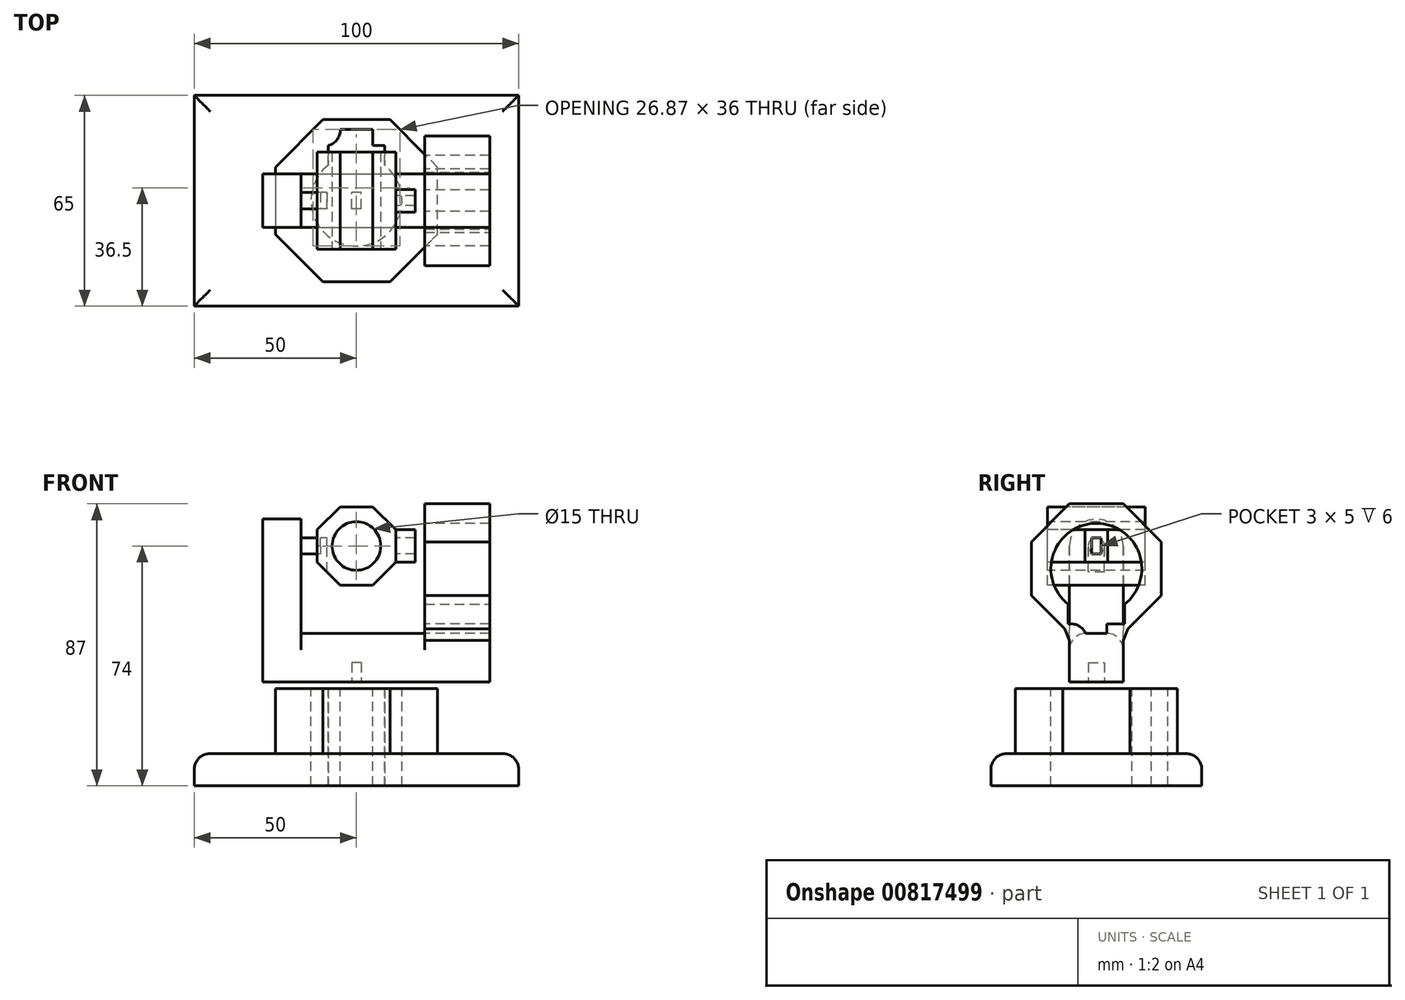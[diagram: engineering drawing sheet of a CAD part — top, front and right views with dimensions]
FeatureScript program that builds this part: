
annotation { "Feature Type Name" : "Feature", "Feature Type Description" : "" }
export const myFeature = defineFeature(function(context is Context, id is Id, definition is map)
    precondition{}
    {
        {
            var Q0;
            Q0=qCreatedBy(makeId("Front.planeOp"),FACE);
            var sketch = newSketch(context, id + "F0", { "sketchPlane" : qUnion([Q0])});
            skCircle(sketch, "E0", {"center": v(0, 0) * mm, "radius": 7.5 * mm});
            skCircle(sketch, "E1.cCircle", {"center": v(0, 0) * mm, "radius": 12.07 * mm, "construction": true});
            skLineSegment(sketch, "E1.0", {"start": v(-5, 12.07) * mm, "end": v(5, 12.07) * mm});
            skLineSegment(sketch, "E1.1", {"start": v(5, 12.07) * mm, "end": v(12.07, 5) * mm});
            skLineSegment(sketch, "E1.2", {"start": v(12.07, 5) * mm, "end": v(12.07, -5) * mm});
            skLineSegment(sketch, "E1.3", {"start": v(12.07, -5) * mm, "end": v(5, -12.07) * mm});
            skLineSegment(sketch, "E1.4", {"start": v(5, -12.07) * mm, "end": v(-5, -12.07) * mm});
            skLineSegment(sketch, "E1.5", {"start": v(-5, -12.07) * mm, "end": v(-12.07, -5) * mm});
            skLineSegment(sketch, "E1.6", {"start": v(-12.07, -5) * mm, "end": v(-12.07, 5) * mm});
            skLineSegment(sketch, "E1.7", {"start": v(-12.07, 5) * mm, "end": v(-5, 12.07) * mm});
            skPoint(sketch, "E1.0.midPoint", {"position": v(0, 12.07) * mm});
            skSolve(sketch);
        }
        {
            var Q0;
            Q0=makeQuery(id+"F0.imprint","IMPRINT",FACE,{"disambiguationData":[TD([[makeQuery(id+"F0.imprint","IMPRINT",EDGE,{"derivedFrom":sQuery(id+"F0.wireOp",EDGE,"E0")}),-1.0]])]});
            extrude(context, id + "F1", {"entities" : qUnion([Q0]), "endBound" : BoundingType.SYMMETRIC, "oppositeDirection" : true, "depth" : 30 * mm, "offsetDistance" : 25 * mm});
        }
        {
            var Q0;
            Q0=makeQuery(id+"F1.opExtrude","SWEPT_FACE",FACE,{"disambiguationData":[OSD([sQuery(id+"F0.wireOp",EDGE,"E1.2")])]});
            var sketch = newSketch(context, id + "F2", { "sketchPlane" : qUnion([Q0])});
            skLineSegment(sketch, "E2.bottom", {"start": v(1.5, 2.5) * mm, "end": v(-1.5, 2.5) * mm});
            skLineSegment(sketch, "E2.top", {"start": v(1.5, -2.5) * mm, "end": v(-1.5, -2.5) * mm});
            skLineSegment(sketch, "E2.left", {"start": v(1.5, 2.5) * mm, "end": v(1.5, -2.5) * mm});
            skLineSegment(sketch, "E2.right", {"start": v(-1.5, 2.5) * mm, "end": v(-1.5, -2.5) * mm});
            skPoint(sketch, "E2.middle", {"position": v(0, 0) * mm});
            skLineSegment(sketch, "E3.bottom", {"start": v(3.5, 5) * mm, "end": v(-3.5, 5) * mm});
            skLineSegment(sketch, "E3.top", {"start": v(3.5, -5) * mm, "end": v(-3.5, -5) * mm});
            skLineSegment(sketch, "E3.left", {"start": v(3.5, 5) * mm, "end": v(3.5, -5) * mm});
            skLineSegment(sketch, "E3.right", {"start": v(-3.5, 5) * mm, "end": v(-3.5, -5) * mm});
            skSolve(sketch);
        }
        {
            var Q0;
            Q0=makeQuery(id+"F2.imprint","IMPRINT",FACE,{"disambiguationData":[TD([[makeQuery(id+"F2.imprint","IMPRINT",EDGE,{"derivedFrom":sQuery(id+"F2.wireOp",EDGE,"E2.bottom")}),-1.0]])]});
            extrude(context, id + "F3", {"entities" : qUnion([Q0]), "operationType" : NewBodyOperationType.ADD, "depth" : 6 * mm, "offsetDistance" : 25 * mm});
        }
        {
            var Q0;
            Q0=makeQuery(id+"F3.opExtrude","CAP_FACE",FACE,{"disambiguationData":[OSD([sQuery(id+"F2.wireOp",EDGE,"E2.bottom"),sQuery(id+"F2.wireOp",EDGE,"E2.top"),sQuery(id+"F2.wireOp",EDGE,"E2.left"),sQuery(id+"F2.wireOp",EDGE,"E2.right"),sQuery(id+"F2.wireOp",EDGE,"E3.bottom"),sQuery(id+"F2.wireOp",EDGE,"E3.top"),sQuery(id+"F2.wireOp",EDGE,"E3.left"),sQuery(id+"F2.wireOp",EDGE,"E3.right")])],"isStart":false});
            var Q1;
            Q1 = qBodyType(qCreatedBy(id + "F5" ,EDGE), BodyType.WIRE);
            cPlane(context, id + "F4", {"entities" : qUnion([Q0, Q1]), "cplaneType" : CPlaneType.OFFSET, "offset" : 3 * mm, "width" : 150 * mm, "height" : 150 * mm});
        }
        {
            var Q0;
            Q0=qCreatedBy(id+"F4.planeOp",FACE);
            var sketch = newSketch(context, id + "F5", { "sketchPlane" : qUnion([Q0])});
            skCircle(sketch, "E4", {"center": v(0, -7) * mm, "radius": 14 * mm});
            skCircle(sketch, "E5.cCircle", {"center": v(0, -7) * mm, "radius": 20 * mm, "construction": true});
            skLineSegment(sketch, "E5.0", {"start": v(-8.28, 13) * mm, "end": v(8.28, 13) * mm});
            skLineSegment(sketch, "E5.1", {"start": v(8.28, 13) * mm, "end": v(20, 1.28) * mm});
            skLineSegment(sketch, "E5.2", {"start": v(20, 1.28) * mm, "end": v(20, -15.28) * mm});
            skLineSegment(sketch, "E5.3", {"start": v(20, -15.28) * mm, "end": v(8.28, -27) * mm});
            skLineSegment(sketch, "E5.4", {"start": v(8.28, -27) * mm, "end": v(-8.28, -27) * mm});
            skLineSegment(sketch, "E5.5", {"start": v(-8.28, -27) * mm, "end": v(-20, -15.28) * mm});
            skLineSegment(sketch, "E5.6", {"start": v(-20, -15.28) * mm, "end": v(-20, 1.28) * mm});
            skLineSegment(sketch, "E5.7", {"start": v(-20, 1.28) * mm, "end": v(-8.28, 13) * mm});
            skPoint(sketch, "E5.0.midPoint", {"position": v(0, 13) * mm});
            skSolve(sketch);
        }
        {
            var Q0;
            Q0=makeQuery(id+"F5.imprint","IMPRINT",FACE,{"disambiguationData":[TD([[makeQuery(id+"F5.imprint","IMPRINT",EDGE,{"derivedFrom":sQuery(id+"F5.wireOp",EDGE,"E4")}),-1.0]])]});
            extrude(context, id + "F6", {"entities" : qUnion([Q0]), "flatOperationType" : FlatOperationType.REMOVE, "depth" : 20 * mm, "offsetDistance" : 25 * mm, "domain" : OperationDomain.MODEL});
        }
        {
            var Q0;
            Q0=makeQuery(id+"F6.opExtrude","CAP_FACE",FACE,{"disambiguationData":[OSD([sQuery(id+"F5.wireOp",EDGE,"E4"),sQuery(id+"F5.wireOp",EDGE,"E5.0"),sQuery(id+"F5.wireOp",EDGE,"E5.1"),sQuery(id+"F5.wireOp",EDGE,"E5.2"),sQuery(id+"F5.wireOp",EDGE,"E5.3"),sQuery(id+"F5.wireOp",EDGE,"E5.4"),sQuery(id+"F5.wireOp",EDGE,"E5.5"),sQuery(id+"F5.wireOp",EDGE,"E5.6"),sQuery(id+"F5.wireOp",EDGE,"E5.7")])],"isStart":false});
            var sketch = newSketch(context, id + "F7", { "sketchPlane" : qUnion([Q0])});
            skLineSegment(sketch, "E6.bottom", {"start": v(8.75, -24) * mm, "end": v(-8.75, -24) * mm});
            skLineSegment(sketch, "E6.top", {"start": v(8.75, -18) * mm, "end": v(-8.75, -18) * mm});
            skLineSegment(sketch, "E6.left", {"start": v(8.75, -24) * mm, "end": v(8.75, -18) * mm});
            skLineSegment(sketch, "E6.right", {"start": v(-8.75, -24) * mm, "end": v(-8.75, -18) * mm});
            skPoint(sketch, "E6.middle", {"position": v(0, -21) * mm});
            skPoint(sketch, "E7", {"position": v(0, 7) * mm});
            skSolve(sketch);
        }
        {
            var Q0;
            Q0=makeQuery(id+"F7.imprint","IMPRINT",FACE,{"disambiguationData":[TD([[makeQuery(id+"F7.imprint","IMPRINT",EDGE,{"derivedFrom":sQuery(id+"F7.wireOp",EDGE,"E6.bottom")}),-1.0]])]});
            var Q1;
            Q1=makeQuery(id+"F6.opExtrude","CAP_FACE",FACE,{"disambiguationData":[OSD([sQuery(id+"F5.wireOp",EDGE,"E4"),sQuery(id+"F5.wireOp",EDGE,"E5.0"),sQuery(id+"F5.wireOp",EDGE,"E5.1"),sQuery(id+"F5.wireOp",EDGE,"E5.2"),sQuery(id+"F5.wireOp",EDGE,"E5.3"),sQuery(id+"F5.wireOp",EDGE,"E5.4"),sQuery(id+"F5.wireOp",EDGE,"E5.5"),sQuery(id+"F5.wireOp",EDGE,"E5.6"),sQuery(id+"F5.wireOp",EDGE,"E5.7")])],"isStart":true});
            extrude(context, id + "F8", {"entities" : qUnion([Q0]), "operationType" : NewBodyOperationType.REMOVE, "endBound" : BoundingType.UP_TO_SURFACE, "oppositeDirection" : true, "depth" : 25 * mm, "endBoundEntityFace" : qUnion([Q1]), "offsetDistance" : 25 * mm});
        }
        {
            var Q0;
            Q0=makeQuery(id+"F6.opExtrude","CAP_FACE",FACE,{"disambiguationData":[OSD([sQuery(id+"F5.wireOp",EDGE,"E4"),sQuery(id+"F5.wireOp",EDGE,"E5.0"),sQuery(id+"F5.wireOp",EDGE,"E5.1"),sQuery(id+"F5.wireOp",EDGE,"E5.2"),sQuery(id+"F5.wireOp",EDGE,"E5.3"),sQuery(id+"F5.wireOp",EDGE,"E5.4"),sQuery(id+"F5.wireOp",EDGE,"E5.5"),sQuery(id+"F5.wireOp",EDGE,"E5.6"),sQuery(id+"F5.wireOp",EDGE,"E5.7")])],"isStart":false});
            var sketch = newSketch(context, id + "F9", { "sketchPlane" : qUnion([Q0])});
            skLineSegment(sketch, "E8.bottom", {"start": v(-8.28, -27) * mm, "end": v(8.28, -27) * mm});
            skLineSegment(sketch, "E8.top", {"start": v(-8.28, -42) * mm, "end": v(8.28, -42) * mm});
            skLineSegment(sketch, "E8.left", {"start": v(-8.28, -27) * mm, "end": v(-8.28, -42) * mm});
            skLineSegment(sketch, "E8.right", {"start": v(8.28, -27) * mm, "end": v(8.28, -42) * mm});
            skSolve(sketch);
        }
        {
            var Q0;
            Q0=makeQuery(id+"F9.imprint","IMPRINT",FACE,{"disambiguationData":[TD([[makeQuery(id+"F9.imprint","IMPRINT",EDGE,{"derivedFrom":sQuery(id+"F9.wireOp",EDGE,"E8.bottom")}),1.0]])]});
            extrude(context, id + "F10", {"entities" : qUnion([Q0]), "operationType" : NewBodyOperationType.ADD, "oppositeDirection" : true, "depth" : 70 * mm, "offsetDistance" : 25 * mm});
        }
        {
            var Q0;
            Q0=makeQuery(id+"F10.opExtrude","CAP_FACE",FACE,{"disambiguationData":[OSD([sQuery(id+"F9.wireOp",EDGE,"E8.bottom"),sQuery(id+"F9.wireOp",EDGE,"E8.top"),sQuery(id+"F9.wireOp",EDGE,"E8.left"),sQuery(id+"F9.wireOp",EDGE,"E8.right")])],"isStart":false});
            var sketch = newSketch(context, id + "F11", { "sketchPlane" : qUnion([Q0])});
            skLineSegment(sketch, "E9.bottom", {"start": v(-8.28, -42) * mm, "end": v(8.28, -42) * mm});
            skLineSegment(sketch, "E9.top", {"start": v(-8.28, 0) * mm, "end": v(8.28, 0) * mm, "construction": true});
            skLineSegment(sketch, "E9.left", {"start": v(-8.28, -42) * mm, "end": v(-8.28, 0) * mm});
            skLineSegment(sketch, "E9.right", {"start": v(8.28, -42) * mm, "end": v(8.28, 0) * mm});
            skArc(sketch, "E10", {"start": v(8.28, 0) * mm, "mid": v(0, 8.28) * mm, "end": v(-8.28, 0) * mm});
            skSolve(sketch);
        }
        {
            var Q0;
            {var subQ2=sQuery(id+"F11.wireOp",EDGE,"E10");Q0=makeQuery(id+"F11.imprint","IMPRINT",FACE,{"disambiguationData":[TD([[makeQuery(id+"F11.imprint","IMPRINT",EDGE,{"derivedFrom":subQ2}),1.0]])]});}
            var Q1;
            Q1=makeQuery(id+"F1.opExtrude","SWEPT_FACE",FACE,{"disambiguationData":[OSD([sQuery(id+"F0.wireOp",EDGE,"E1.6")])]});
            extrude(context, id + "F12", {"entities" : qUnion([Q0]), "operationType" : NewBodyOperationType.ADD, "endBound" : BoundingType.UP_TO_SURFACE, "oppositeDirection" : true, "depth" : 5 * mm, "endBoundEntityFace" : qUnion([Q1]), "hasOffset" : true, "offsetDistance" : 5 * mm});
        }
        {
            var Q0;
            Q0=makeQuery(id+"F10.opExtrude","SWEPT_FACE",FACE,{"disambiguationData":[OSD([sQuery(id+"F9.wireOp",EDGE,"E8.top")])]});
            var sketch = newSketch(context, id + "F13", { "sketchPlane" : qUnion([Q0])});
            skLineSegment(sketch, "E11.bottom", {"start": v(1.5, 2.5) * mm, "end": v(-1.5, 2.5) * mm});
            skLineSegment(sketch, "E11.top", {"start": v(1.5, -2.5) * mm, "end": v(-1.5, -2.5) * mm});
            skLineSegment(sketch, "E11.left", {"start": v(1.5, 2.5) * mm, "end": v(1.5, -2.5) * mm});
            skLineSegment(sketch, "E11.right", {"start": v(-1.5, 2.5) * mm, "end": v(-1.5, -2.5) * mm});
            skPoint(sketch, "E11.middle", {"position": v(0, 0) * mm});
            skSolve(sketch);
        }
        {
            var Q0;
            Q0=makeQuery(id+"F13.imprint","IMPRINT",FACE,{"disambiguationData":[TD([[makeQuery(id+"F13.imprint","IMPRINT",EDGE,{"derivedFrom":sQuery(id+"F13.wireOp",EDGE,"E11.bottom")}),1.0]])]});
            var Q1;
            Q1=makeQuery(id+"F10.opExtrude","SWEPT_FACE",FACE,{"disambiguationData":[OSD([sQuery(id+"F9.wireOp",EDGE,"E8.bottom")])]});
            extrude(context, id + "F14", {"entities" : qUnion([Q0]), "operationType" : NewBodyOperationType.REMOVE, "oppositeDirection" : true, "depth" : 6 * mm, "endBoundEntityFace" : qUnion([Q1]), "hasOffset" : true, "offsetDistance" : 2 * mm});
        }
        {
            var Q0;
            Q0=makeQuery(id+"F10.opExtrude","SWEPT_FACE",FACE,{"disambiguationData":[OSD([sQuery(id+"F9.wireOp",EDGE,"E8.top")])]});
            cPlane(context, id + "F15", {"entities" : qUnion([Q0]), "cplaneType" : CPlaneType.OFFSET, "offset" : 2 * mm, "width" : 150 * mm, "height" : 150 * mm});
        }
        {
            var Q0;
            Q0=qCreatedBy(id+"F15.planeOp",FACE);
            var sketch = newSketch(context, id + "F16", { "sketchPlane" : qUnion([Q0])});
            skCircle(sketch, "E12", {"center": v(0, 0) * mm, "radius": 14 * mm});
            skCircle(sketch, "E13.cCircle", {"center": v(0, 0) * mm, "radius": 25 * mm, "construction": true});
            skLineSegment(sketch, "E13.0", {"start": v(-10.36, 25) * mm, "end": v(10.36, 25) * mm});
            skLineSegment(sketch, "E13.1", {"start": v(10.36, 25) * mm, "end": v(25, 10.36) * mm});
            skLineSegment(sketch, "E13.2", {"start": v(25, 10.36) * mm, "end": v(25, -10.36) * mm});
            skLineSegment(sketch, "E13.3", {"start": v(25, -10.36) * mm, "end": v(10.36, -25) * mm});
            skLineSegment(sketch, "E13.4", {"start": v(10.36, -25) * mm, "end": v(-10.36, -25) * mm});
            skLineSegment(sketch, "E13.5", {"start": v(-10.36, -25) * mm, "end": v(-25, -10.36) * mm});
            skLineSegment(sketch, "E13.6", {"start": v(-25, -10.36) * mm, "end": v(-25, 10.36) * mm});
            skLineSegment(sketch, "E13.7", {"start": v(-25, 10.36) * mm, "end": v(-10.36, 25) * mm});
            skPoint(sketch, "E13.0.midPoint", {"position": v(0, 25) * mm});
            skSolve(sketch);
        }
        {
            var Q0;
            Q0=makeQuery(id+"F16.imprint","IMPRINT",FACE,{"disambiguationData":[TD([[makeQuery(id+"F16.imprint","IMPRINT",EDGE,{"derivedFrom":sQuery(id+"F16.wireOp",EDGE,"ab7be03b-d63e-4127-b53d-c97241b83293.bottom")}),-1.0]])]});
            var Q1;
            Q1=makeQuery(id+"F16.imprint","IMPRINT",FACE,{"disambiguationData":[TD([[makeQuery(id+"F16.imprint","IMPRINT",EDGE,{"derivedFrom":sQuery(id+"F16.wireOp",EDGE,"E12")}),-1.0]])]});
            extrude(context, id + "F17", {"entities" : qUnion([Q0, Q1]), "depth" : 20 * mm, "offsetDistance" : 25 * mm});
        }
        {
            var Q0;
            Q0=makeQuery(id+"F17.opExtrude","CAP_FACE",FACE,{"disambiguationData":[OSD([sQuery(id+"F16.wireOp",EDGE,"E12"),sQuery(id+"F16.wireOp",EDGE,"E13.0"),sQuery(id+"F16.wireOp",EDGE,"E13.1"),sQuery(id+"F16.wireOp",EDGE,"E13.2"),sQuery(id+"F16.wireOp",EDGE,"E13.3"),sQuery(id+"F16.wireOp",EDGE,"E13.4"),sQuery(id+"F16.wireOp",EDGE,"E13.5"),sQuery(id+"F16.wireOp",EDGE,"E13.6"),sQuery(id+"F16.wireOp",EDGE,"E13.7")])],"isStart":false});
            var sketch = newSketch(context, id + "F18", { "sketchPlane" : qUnion([Q0])});
            skLineSegment(sketch, "E14.bottom", {"start": v(8.75, -17) * mm, "end": v(-8.75, -17) * mm});
            skLineSegment(sketch, "E14.top", {"start": v(8.75, -11) * mm, "end": v(-8.75, -11) * mm});
            skLineSegment(sketch, "E14.left", {"start": v(8.75, -17) * mm, "end": v(8.75, -11) * mm});
            skLineSegment(sketch, "E14.right", {"start": v(-8.75, -17) * mm, "end": v(-8.75, -11) * mm});
            skPoint(sketch, "E14.middle", {"position": v(0, -14) * mm});
            skPoint(sketch, "E15", {"position": v(-27.27, 14.01) * mm});
            skSolve(sketch);
        }
        {
            var Q0;
            Q0 = qSketchRegion(id + "F18", true);
            var Q1;
            Q1=makeQuery(id+"F17.opExtrude","CAP_FACE",FACE,{"disambiguationData":[OSD([sQuery(id+"F16.wireOp",EDGE,"E12"),sQuery(id+"F16.wireOp",EDGE,"E13.0"),sQuery(id+"F16.wireOp",EDGE,"E13.1"),sQuery(id+"F16.wireOp",EDGE,"E13.2"),sQuery(id+"F16.wireOp",EDGE,"E13.3"),sQuery(id+"F16.wireOp",EDGE,"E13.4"),sQuery(id+"F16.wireOp",EDGE,"E13.5"),sQuery(id+"F16.wireOp",EDGE,"E13.6"),sQuery(id+"F16.wireOp",EDGE,"E13.7")])],"isStart":true});
            extrude(context, id + "F19", {"entities" : qUnion([Q0]), "operationType" : NewBodyOperationType.REMOVE, "endBound" : BoundingType.UP_TO_SURFACE, "oppositeDirection" : true, "depth" : 25 * mm, "endBoundEntityFace" : qUnion([Q1]), "offsetDistance" : 25 * mm});
        }
        {
            var Q0;
            Q0=makeQuery(id+"F1.opExtrude","SWEPT_FACE",FACE,{"disambiguationData":[OSD([sQuery(id+"F0.wireOp",EDGE,"E1.6")])]});
            var sketch = newSketch(context, id + "F20", { "sketchPlane" : qUnion([Q0])});
            skCircle(sketch, "E16", {"center": v(0, 0) * mm, "radius": 2.5 * mm});
            skSolve(sketch);
        }
        {
            var Q0;
            Q0=makeQuery(id+"F20.imprint","IMPRINT",FACE,{"disambiguationData":[TD([[makeQuery(id+"F20.imprint","IMPRINT",EDGE,{"derivedFrom":sQuery(id+"F20.wireOp",EDGE,"E16")}),1.0]])]});
            var Q1;
            Q1=makeQuery(id+"F1.opExtrude","SWEPT_FACE",FACE,{"disambiguationData":[OSD([sQuery(id+"F0.wireOp",EDGE,"E0")])]});
            extrude(context, id + "F21", {"entities" : qUnion([Q0]), "operationType" : NewBodyOperationType.REMOVE, "oppositeDirection" : true, "depth" : 3 * mm, "endBoundEntityFace" : qUnion([Q1]), "offsetDistance" : 1 * mm});
        }
        {
            var Q0;
            Q0=makeQuery(id+"F12.opExtrude","CAP_FACE",FACE,{"disambiguationData":[OSD([sQuery(id+"F9.wireOp",EDGE,"E8.bottom"),sQuery(id+"F11.wireOp",EDGE,"E9.left"),sQuery(id+"F11.wireOp",EDGE,"E9.right"),sQuery(id+"F11.wireOp",EDGE,"E10")])],"isStart":false});
            var sketch = newSketch(context, id + "F22", { "sketchPlane" : qUnion([Q0])});
            skCircle(sketch, "E17", {"center": v(0, 0) * mm, "radius": 2.5 * mm});
            skSolve(sketch);
        }
        {
            var Q0;
            Q0 = qSketchRegion(id + "F22", true);
            var Q1;
            Q1=sQuery(id+"F22.wireOp",EDGE,"E17");
            var Q2;
            Q2=makeQuery(id+"F21.boolean.opBoolean","COPY",FACE,{"derivedFrom":makeQuery(id+"F21.opExtrude","CAP_FACE",FACE,{"disambiguationData":[OSD([sQuery(id+"F20.wireOp",EDGE,"E16")])],"isStart":false})});
            extrude(context, id + "F23", {"entities" : qUnion([Q0]), "operationType" : NewBodyOperationType.ADD, "surfaceEntities" : qUnion([Q1]), "endBound" : BoundingType.UP_TO_SURFACE, "depth" : 25 * mm, "endBoundEntityFace" : qUnion([Q2]), "hasOffset" : true, "offsetDistance" : 2 * mm});
        }
        {
            var Q0;
            Q0=makeQuery(id+"F1.opExtrude","SWEPT_FACE",FACE,{"disambiguationData":[OSD([sQuery(id+"F0.wireOp",EDGE,"E1.6")])]});
            var sketch = newSketch(context, id + "F24", { "sketchPlane" : qUnion([Q0])});
            skLineSegment(sketch, "E18.bottom", {"start": v(-2.5, 0) * mm, "end": v(2.5, 0) * mm});
            skLineSegment(sketch, "E18.top", {"start": v(-2.5, -12.07) * mm, "end": v(2.5, -12.07) * mm});
            skLineSegment(sketch, "E18.left", {"start": v(-2.5, 0) * mm, "end": v(-2.5, -12.07) * mm});
            skLineSegment(sketch, "E18.right", {"start": v(2.5, 0) * mm, "end": v(2.5, -12.07) * mm});
            skSolve(sketch);
        }
        {
            var Q0;
            {var subQ0=sQuery(id+"F24.wireOp",EDGE,"E18.left");var subQ1=sQuery(id+"F24.wireOp",EDGE,"E18.bottom");var subQ2=makeQuery(id+"F21.boolean.opBoolean","COPY",EDGE,{"derivedFrom":makeQuery(id+"F21.opExtrude","CAP_EDGE",EDGE,{"disambiguationData":[OSD([sQuery(id+"F20.wireOp",EDGE,"E16")])],"isStart":true})});var subQ3=makeQuery(id+"F24.imprint","INTERSECT",VERTEX,{"derivedFrom":[subQ2,subQ1,subQ0]});Q0=makeQuery(id+"F24.imprint","IMPRINT",FACE,{"disambiguationData":[TD([[makeQuery(id+"F24.imprint","IMPRINT",EDGE,{"disambiguationData":[TD([[subQ3,-1.0]])],"derivedFrom":subQ0}),1.0]])]});}
            var Q1;
            {var subQ0=sQuery(id+"F24.wireOp",EDGE,"E18.top");Q1=makeQuery(id+"F24.imprint","IMPRINT",FACE,{"disambiguationData":[TD([[makeQuery(id+"F24.imprint","IMPRINT",EDGE,{"derivedFrom":subQ0}),1.0]])]});}
            var Q2;
            Q2=makeQuery(id+"F21.boolean.opBoolean","COPY",FACE,{"derivedFrom":makeQuery(id+"F21.opExtrude","CAP_FACE",FACE,{"disambiguationData":[OSD([sQuery(id+"F20.wireOp",EDGE,"E16")])],"isStart":false})});
            extrude(context, id + "F25", {"entities" : qUnion([Q0, Q1]), "operationType" : NewBodyOperationType.REMOVE, "endBound" : BoundingType.UP_TO_SURFACE, "oppositeDirection" : true, "depth" : 25 * mm, "endBoundEntityFace" : qUnion([Q2]), "offsetDistance" : 25 * mm});
        }
        {
            var Q0;
            Q0=makeQuery(id+"F17.opExtrude","CAP_FACE",FACE,{"disambiguationData":[OSD([sQuery(id+"F16.wireOp",EDGE,"E12"),sQuery(id+"F16.wireOp",EDGE,"E13.0"),sQuery(id+"F16.wireOp",EDGE,"E13.1"),sQuery(id+"F16.wireOp",EDGE,"E13.2"),sQuery(id+"F16.wireOp",EDGE,"E13.3"),sQuery(id+"F16.wireOp",EDGE,"E13.4"),sQuery(id+"F16.wireOp",EDGE,"E13.5"),sQuery(id+"F16.wireOp",EDGE,"E13.6"),sQuery(id+"F16.wireOp",EDGE,"E13.7")])],"isStart":false});
            var sketch = newSketch(context, id + "F26", { "sketchPlane" : qUnion([Q0])});
            skLineSegment(sketch, "E19.bottom", {"start": v(50, 32.5) * mm, "end": v(-50, 32.5) * mm});
            skLineSegment(sketch, "E19.top", {"start": v(50, -32.5) * mm, "end": v(-50, -32.5) * mm});
            skLineSegment(sketch, "E19.left", {"start": v(50, 32.5) * mm, "end": v(50, -32.5) * mm});
            skLineSegment(sketch, "E19.right", {"start": v(-50, 32.5) * mm, "end": v(-50, -32.5) * mm});
            skPoint(sketch, "E19.middle", {"position": v(0, 0) * mm});
            skSolve(sketch);
        }
        {
            var Q0;
            Q0=makeQuery(id+"F26.imprint","IMPRINT",FACE,{"disambiguationData":[TD([[makeQuery(id+"F26.imprint","IMPRINT",EDGE,{"derivedFrom":sQuery(id+"F26.wireOp",EDGE,"E19.bottom")}),1.0]])]});
            var Q1;
            {var subQ5=sQuery(id+"F16.wireOp",EDGE,"E13.0");Q1=makeQuery(id+"F26.imprint","IMPRINT",FACE,{"disambiguationData":[TD([[makeQuery(id+"F26.imprint","IMPRINT",EDGE,{"derivedFrom":makeQuery(id+"F17.opExtrude","CAP_EDGE",EDGE,{"disambiguationData":[OSD([subQ5])],"isStart":false})}),-1.0]])]});}
            extrude(context, id + "F27", {"entities" : qUnion([Q0, Q1]), "operationType" : NewBodyOperationType.ADD, "depth" : 10 * mm, "offsetDistance" : 25 * mm});
        }
        {
            var Q0;
            Q0=makeQuery(id+"F27.opExtrude","CAP_EDGE",EDGE,{"disambiguationData":[OSD([sQuery(id+"F26.wireOp",EDGE,"E19.left")])],"isStart":true});
            var Q1;
            Q1=makeQuery(id+"F27.opExtrude","CAP_EDGE",EDGE,{"disambiguationData":[OSD([sQuery(id+"F26.wireOp",EDGE,"E19.bottom")])],"isStart":true});
            var Q2;
            Q2=makeQuery(id+"F27.opExtrude","CAP_EDGE",EDGE,{"disambiguationData":[OSD([sQuery(id+"F26.wireOp",EDGE,"E19.right")])],"isStart":true});
            var Q3;
            Q3=makeQuery(id+"F27.opExtrude","CAP_EDGE",EDGE,{"disambiguationData":[OSD([sQuery(id+"F26.wireOp",EDGE,"E19.top")])],"isStart":true});
            fillet(context, id + "F28", {"entities" : qUnion([Q0, Q1, Q2, Q3]), "radius" : 5 * mm, "tangentPropagation" : true, "allowEdgeOverflow" : false});
        }
        {
            var Q0;
            Q0=makeQuery(id+"F10.boolean.opBoolean","SPLIT",EDGE,{"derivedFrom":makeQuery(id+"F10.opExtrude","SWEPT_EDGE",EDGE,{"disambiguationData":[OSD([sQuery(id+"F5.wireOp",EDGE,"E5.5"),sQuery(id+"F9.wireOp",EDGE,"E8.bottom"),sQuery(id+"F9.wireOp",EDGE,"E8.left")])]})});
            var Q1;
            Q1=makeQuery(id+"F10.boolean.opBoolean","SPLIT",EDGE,{"derivedFrom":makeQuery(id+"F10.opExtrude","SWEPT_EDGE",EDGE,{"disambiguationData":[OSD([sQuery(id+"F5.wireOp",EDGE,"E5.3"),sQuery(id+"F9.wireOp",EDGE,"E8.bottom"),sQuery(id+"F9.wireOp",EDGE,"E8.right")])]})});
            fillet(context, id + "F29", {"entities" : qUnion([Q0, Q1]), "radius" : 5 * mm, "tangentPropagation" : true, "allowEdgeOverflow" : false});
        }
        {
            var Q0;
            {var subQ0=sQuery(id+"F5.wireOp",EDGE,"E5.3");Q0=makeQuery(id+"F10.boolean.opBoolean","MERGE",EDGE,{"derivedFrom":[makeQuery(id+"F6.opExtrude","SWEPT_EDGE",EDGE,{"disambiguationData":[OSD([subQ0,sQuery(id+"F5.wireOp",EDGE,"E5.4")])]}),makeQuery(id+"F10.opExtrude","SWEPT_EDGE",EDGE,{"disambiguationData":[OSD([subQ0,sQuery(id+"F9.wireOp",EDGE,"E8.bottom"),sQuery(id+"F9.wireOp",EDGE,"E8.right")])]})]});}
            var Q1;
            {var subQ0=sQuery(id+"F5.wireOp",EDGE,"E5.5");Q1=makeQuery(id+"F10.boolean.opBoolean","MERGE",EDGE,{"derivedFrom":[makeQuery(id+"F6.opExtrude","SWEPT_EDGE",EDGE,{"disambiguationData":[OSD([sQuery(id+"F5.wireOp",EDGE,"E5.4"),subQ0])]}),makeQuery(id+"F10.opExtrude","SWEPT_EDGE",EDGE,{"disambiguationData":[OSD([subQ0,sQuery(id+"F9.wireOp",EDGE,"E8.bottom"),sQuery(id+"F9.wireOp",EDGE,"E8.left")])]})]});}
            chamfer(context, id + "F30", {"entities" : qUnion([Q0, Q1]), "width" : 5 * mm, "tangentPropagation" : true});
        }
        {
            var Q0;
            Q0=makeQuery(id+"F6.opExtrude","CAP_FACE",FACE,{"disambiguationData":[OSD([sQuery(id+"F5.wireOp",EDGE,"E4"),sQuery(id+"F5.wireOp",EDGE,"E5.0"),sQuery(id+"F5.wireOp",EDGE,"E5.1"),sQuery(id+"F5.wireOp",EDGE,"E5.2"),sQuery(id+"F5.wireOp",EDGE,"E5.3"),sQuery(id+"F5.wireOp",EDGE,"E5.4"),sQuery(id+"F5.wireOp",EDGE,"E5.5"),sQuery(id+"F5.wireOp",EDGE,"E5.6"),sQuery(id+"F5.wireOp",EDGE,"E5.7")])],"isStart":true});
            var sketch = newSketch(context, id + "F31", { "sketchPlane" : qUnion([Q0])});
            skLineSegment(sketch, "E20.bottom", {"start": v(-3.28, -24) * mm, "end": v(3.28, -24) * mm});
            skLineSegment(sketch, "E20.top", {"start": v(-3.28, -27) * mm, "end": v(3.28, -27) * mm});
            skLineSegment(sketch, "E20.left", {"start": v(-3.28, -24) * mm, "end": v(-3.28, -27) * mm});
            skLineSegment(sketch, "E20.right", {"start": v(3.28, -24) * mm, "end": v(3.28, -27) * mm});
            skSolve(sketch);
        }
        {
            var Q0;
            Q0 = qSketchRegion(id + "F31", true);
            var Q1;
            Q1=makeQuery(id+"F10.boolean.opBoolean","MERGE",FACE,{"derivedFrom":[makeQuery(id+"F6.opExtrude","CAP_FACE",FACE,{"disambiguationData":[OSD([sQuery(id+"F5.wireOp",EDGE,"E4"),sQuery(id+"F5.wireOp",EDGE,"E5.0"),sQuery(id+"F5.wireOp",EDGE,"E5.1"),sQuery(id+"F5.wireOp",EDGE,"E5.2"),sQuery(id+"F5.wireOp",EDGE,"E5.3"),sQuery(id+"F5.wireOp",EDGE,"E5.4"),sQuery(id+"F5.wireOp",EDGE,"E5.5"),sQuery(id+"F5.wireOp",EDGE,"E5.6"),sQuery(id+"F5.wireOp",EDGE,"E5.7")])],"isStart":false}),makeQuery(id+"F10.opExtrude","CAP_FACE",FACE,{"disambiguationData":[OSD([sQuery(id+"F9.wireOp",EDGE,"E8.bottom"),sQuery(id+"F9.wireOp",EDGE,"E8.top"),sQuery(id+"F9.wireOp",EDGE,"E8.left"),sQuery(id+"F9.wireOp",EDGE,"E8.right")])],"isStart":true})]});
            extrude(context, id + "F32", {"entities" : qUnion([Q0]), "operationType" : NewBodyOperationType.REMOVE, "endBound" : BoundingType.UP_TO_SURFACE, "oppositeDirection" : true, "depth" : 25 * mm, "endBoundEntityFace" : qUnion([Q1]), "offsetDistance" : 25 * mm});
        }
        {
            var Q0;
            Q0=makeQuery(id+"F32.boolean.opBoolean","COPY",EDGE,{"derivedFrom":makeQuery(id+"F32.opExtrude","SWEPT_EDGE",EDGE,{"disambiguationData":[OSD([sQuery(id+"F7.wireOp",EDGE,"E6.bottom"),sQuery(id+"F31.wireOp",EDGE,"E20.bottom"),sQuery(id+"F31.wireOp",EDGE,"E20.left")])]})});
            var Q1;
            Q1=makeQuery(id+"F32.boolean.opBoolean","COPY",EDGE,{"derivedFrom":makeQuery(id+"F32.opExtrude","SWEPT_EDGE",EDGE,{"disambiguationData":[OSD([sQuery(id+"F7.wireOp",EDGE,"E6.bottom"),sQuery(id+"F31.wireOp",EDGE,"E20.bottom"),sQuery(id+"F31.wireOp",EDGE,"E20.right")])]})});
            fillet(context, id + "F33", {"entities" : qUnion([Q0, Q1]), "radius" : 5 * mm, "tangentPropagation" : true, "allowEdgeOverflow" : false});
        }
        {
            var Q0;
            Q0=makeQuery(id+"F17.opExtrude","CAP_FACE",FACE,{"disambiguationData":[OSD([sQuery(id+"F16.wireOp",EDGE,"E12"),sQuery(id+"F16.wireOp",EDGE,"E13.0"),sQuery(id+"F16.wireOp",EDGE,"E13.1"),sQuery(id+"F16.wireOp",EDGE,"E13.2"),sQuery(id+"F16.wireOp",EDGE,"E13.3"),sQuery(id+"F16.wireOp",EDGE,"E13.4"),sQuery(id+"F16.wireOp",EDGE,"E13.5"),sQuery(id+"F16.wireOp",EDGE,"E13.6"),sQuery(id+"F16.wireOp",EDGE,"E13.7")])],"isStart":true});
            var sketch = newSketch(context, id + "F34", { "sketchPlane" : qUnion([Q0])});
            skLineSegment(sketch, "E21.bottom", {"start": v(5, 22) * mm, "end": v(-5, 22) * mm});
            skLineSegment(sketch, "E21.top", {"start": v(5, 17) * mm, "end": v(-5, 17) * mm});
            skLineSegment(sketch, "E21.left", {"start": v(5, 22) * mm, "end": v(5, 17) * mm});
            skLineSegment(sketch, "E21.right", {"start": v(-5, 22) * mm, "end": v(-5, 17) * mm});
            skPoint(sketch, "E21.middle", {"position": v(0, 19.5) * mm});
            skSolve(sketch);
        }
        {
            var Q0;
            Q0 = qSketchRegion(id + "F34", true);
            var Q1;
            Q1=makeQuery(id+"F27.opExtrude","CAP_FACE",FACE,{"disambiguationData":[OSD([sQuery(id+"F16.wireOp",EDGE,"E12"),sQuery(id+"F18.wireOp",EDGE,"E14.bottom"),sQuery(id+"F18.wireOp",EDGE,"E14.top"),sQuery(id+"F18.wireOp",EDGE,"E14.left"),sQuery(id+"F18.wireOp",EDGE,"E14.right"),sQuery(id+"F26.wireOp",EDGE,"E19.bottom"),sQuery(id+"F26.wireOp",EDGE,"E19.top"),sQuery(id+"F26.wireOp",EDGE,"E19.left"),sQuery(id+"F26.wireOp",EDGE,"E19.right")])],"isStart":false});
            extrude(context, id + "F35", {"entities" : qUnion([Q0]), "operationType" : NewBodyOperationType.REMOVE, "endBound" : BoundingType.UP_TO_SURFACE, "oppositeDirection" : true, "depth" : 25 * mm, "endBoundEntityFace" : qUnion([Q1]), "offsetDistance" : 25 * mm});
        }
        {
            var Q0;
            Q0=makeQuery(id+"F35.boolean.opBoolean","COPY",EDGE,{"derivedFrom":makeQuery(id+"F35.opExtrude","SWEPT_EDGE",EDGE,{"disambiguationData":[OSD([sQuery(id+"F18.wireOp",EDGE,"E14.bottom"),sQuery(id+"F34.wireOp",EDGE,"E21.top"),sQuery(id+"F34.wireOp",EDGE,"E21.left")])]})});
            var Q1;
            Q1=makeQuery(id+"F35.boolean.opBoolean","COPY",EDGE,{"derivedFrom":makeQuery(id+"F35.opExtrude","SWEPT_EDGE",EDGE,{"disambiguationData":[OSD([sQuery(id+"F18.wireOp",EDGE,"E14.bottom"),sQuery(id+"F34.wireOp",EDGE,"E21.top"),sQuery(id+"F34.wireOp",EDGE,"E21.right")])]})});
            fillet(context, id + "F36", {"entities" : qUnion([Q0, Q1]), "radius" : 5 * mm, "tangentPropagation" : true, "allowEdgeOverflow" : false});
        }
    });
